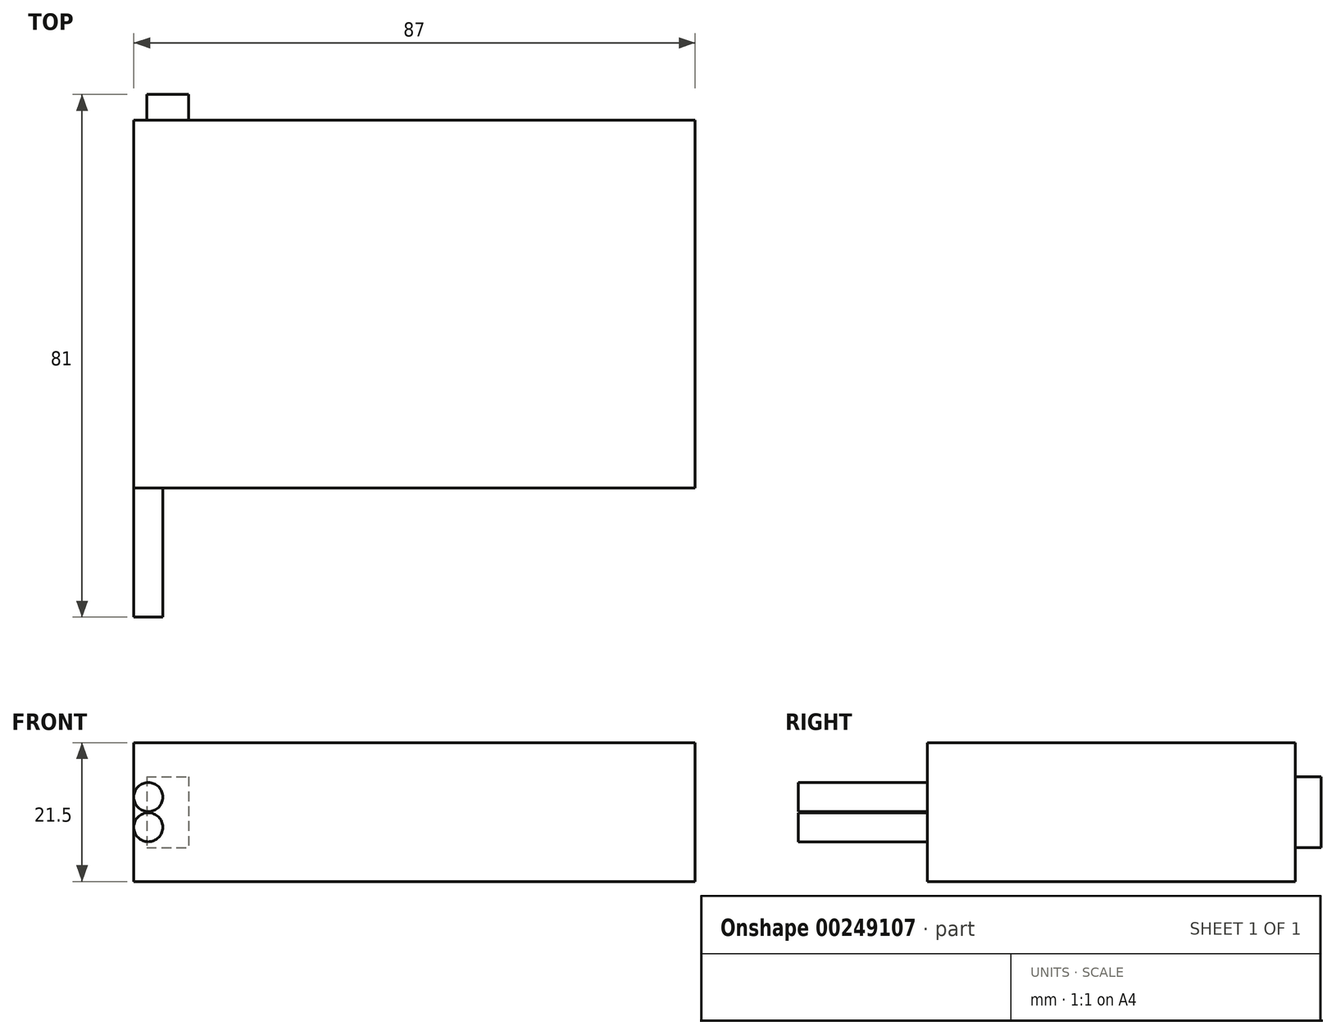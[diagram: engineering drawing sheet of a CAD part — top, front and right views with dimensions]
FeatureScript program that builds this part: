
annotation { "Feature Type Name" : "Feature", "Feature Type Description" : "" }
export const myFeature = defineFeature(function(context is Context, id is Id, definition is map)
    precondition{}
    {
        {
            var Q0;
            Q0=qCreatedBy(makeId("Top.planeOp"),FACE);
            var sketch = newSketch(context, id + "F0", { "sketchPlane" : qUnion([Q0])});
            skLineSegment(sketch, "E0.bottom", {"start": v(-43.5, 28.5) * mm, "end": v(43.5, 28.5) * mm});
            skLineSegment(sketch, "E0.top", {"start": v(-43.5, -28.5) * mm, "end": v(43.5, -28.5) * mm});
            skLineSegment(sketch, "E0.left", {"start": v(-43.5, 28.5) * mm, "end": v(-43.5, -28.5) * mm});
            skLineSegment(sketch, "E0.right", {"start": v(43.5, 28.5) * mm, "end": v(43.5, -28.5) * mm});
            skSolve(sketch);
        }
        {
            var Q0;
            Q0=makeQuery(id+"F0.imprint","IMPRINT",FACE,{"disambiguationData":[TD([[makeQuery(id+"F0.imprint","IMPRINT",EDGE,{"derivedFrom":sQuery(id+"F0.wireOp",EDGE,"E0.bottom")}),-1.0]])]});
            extrude(context, id + "F1", {"entities" : qUnion([Q0]), "depth" : 21.5 * mm});
        }
        {
            var Q0;
            Q0=makeQuery(id+"F1.opExtrude","SWEPT_FACE",FACE,{"disambiguationData":[OSD([sQuery(id+"F0.wireOp",EDGE,"E0.top")])]});
            var sketch = newSketch(context, id + "F2", { "sketchPlane" : qUnion([Q0])});
            skCircle(sketch, "E1", {"center": v(-41.25, 13.09) * mm, "radius": 2.25 * mm});
            skCircle(sketch, "E2", {"center": v(-41.25, 8.41) * mm, "radius": 2.25 * mm});
            skLineSegment(sketch, "E3", {"start": v(-29.01, 10.75) * mm, "end": v(-2.7, 10.75) * mm, "construction": true});
            skSolve(sketch);
        }
        {
            var Q0;
            Q0=makeQuery(id+"F2.imprint","IMPRINT",FACE,{"disambiguationData":[TD([[makeQuery(id+"F2.imprint","IMPRINT",EDGE,{"derivedFrom":sQuery(id+"F2.wireOp",EDGE,"E1")}),1.0]])]});
            var Q1;
            Q1=makeQuery(id+"F2.imprint","IMPRINT",FACE,{"disambiguationData":[TD([[makeQuery(id+"F2.imprint","IMPRINT",EDGE,{"derivedFrom":sQuery(id+"F2.wireOp",EDGE,"E2")}),1.0]])]});
            extrude(context, id + "F3", {"entities" : qUnion([Q0, Q1]), "depth" : 20 * mm});
        }
        {
            var Q0;
            Q0=makeQuery(id+"F1.opExtrude","SWEPT_FACE",FACE,{"disambiguationData":[OSD([sQuery(id+"F0.wireOp",EDGE,"E0.bottom")])]});
            var sketch = newSketch(context, id + "F4", { "sketchPlane" : qUnion([Q0])});
            skLineSegment(sketch, "E4.bottom", {"start": v(41.5, 16.25) * mm, "end": v(35, 16.25) * mm});
            skLineSegment(sketch, "E4.top", {"start": v(41.5, 5.25) * mm, "end": v(35, 5.25) * mm});
            skLineSegment(sketch, "E4.left", {"start": v(41.5, 16.25) * mm, "end": v(41.5, 5.25) * mm});
            skLineSegment(sketch, "E4.right", {"start": v(35, 16.25) * mm, "end": v(35, 5.25) * mm});
            skLineSegment(sketch, "E5", {"start": v(-24.9, 10.75) * mm, "end": v(0, 10.75) * mm, "construction": true});
            skSolve(sketch);
        }
        {
            var Q0;
            Q0=makeQuery(id+"F4.imprint","IMPRINT",FACE,{"disambiguationData":[TD([[makeQuery(id+"F4.imprint","IMPRINT",EDGE,{"derivedFrom":sQuery(id+"F4.wireOp",EDGE,"E4.bottom")}),1.0]])]});
            extrude(context, id + "F5", {"entities" : qUnion([Q0]), "depth" : 4 * mm});
        }
    });
